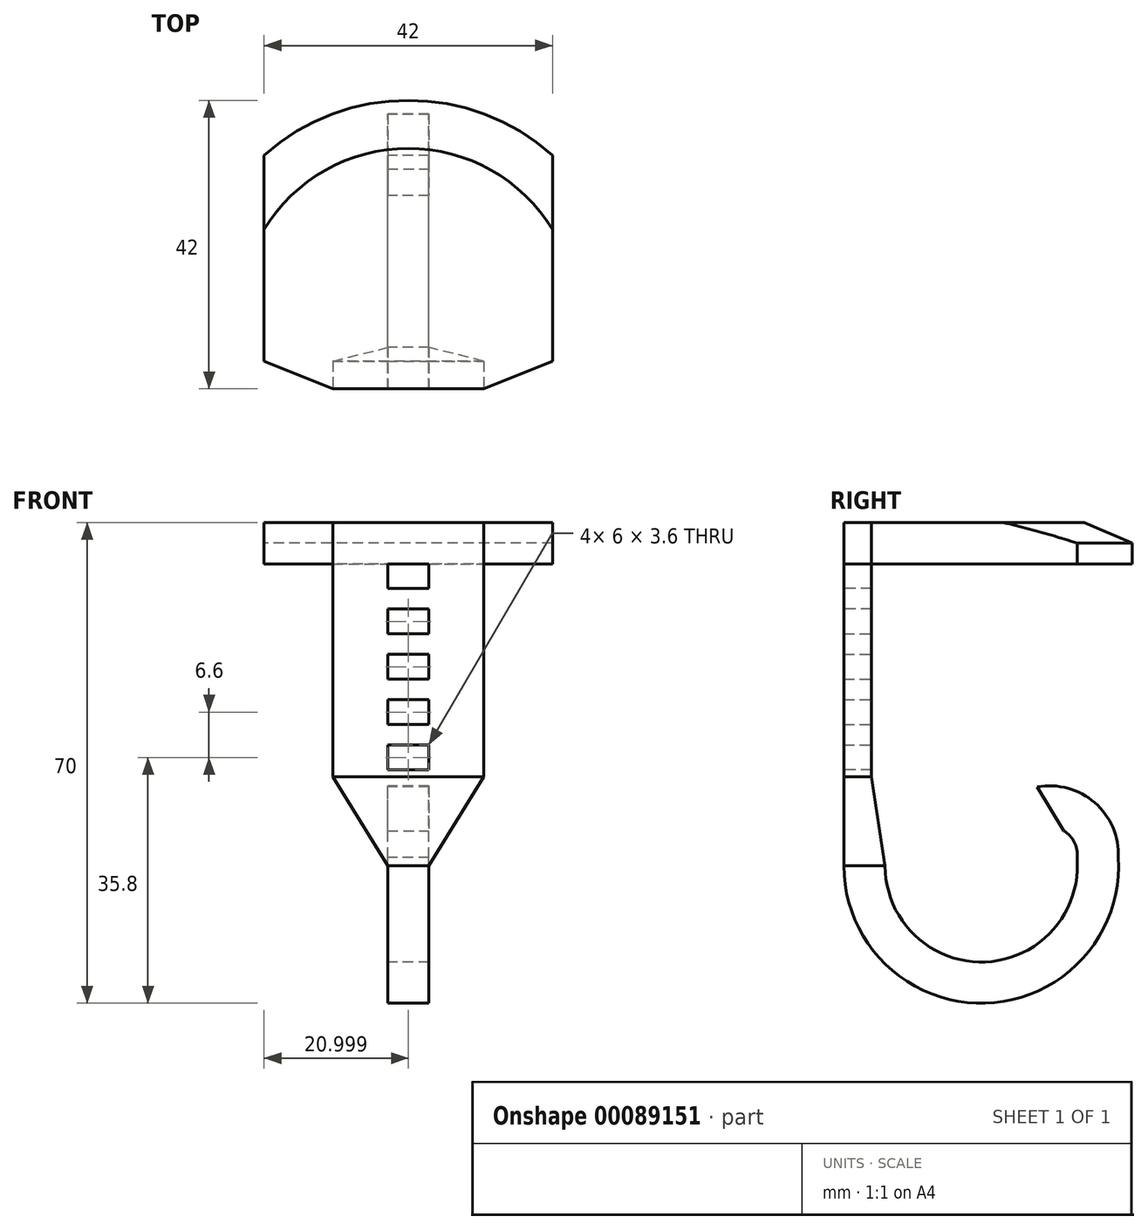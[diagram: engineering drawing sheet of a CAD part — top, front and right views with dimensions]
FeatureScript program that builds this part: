
annotation { "Feature Type Name" : "Feature", "Feature Type Description" : "" }
export const myFeature = defineFeature(function(context is Context, id is Id, definition is map)
    precondition{}
    {
        {
            var Q0;
            Q0=qCreatedBy(makeId("Top.planeOp"),FACE);
            var sketch = newSketch(context, id + "F0", { "sketchPlane" : qUnion([Q0])});
            skLineSegment(sketch, "E0.bottom", {"start": v(-37.77, 36.59) * mm, "end": v(4.23, 36.59) * mm});
            skLineSegment(sketch, "E0.top", {"start": v(-37.77, -1.41) * mm, "end": v(4.23, -1.41) * mm});
            skLineSegment(sketch, "E0.left", {"start": v(-37.77, 36.59) * mm, "end": v(-37.77, -1.41) * mm});
            skLineSegment(sketch, "E0.right", {"start": v(4.23, 36.59) * mm, "end": v(4.23, -1.41) * mm});
            skLineSegment(sketch, "E1", {"start": v(-16.77, 36.59) * mm, "end": v(-16.77, -1.41) * mm, "construction": true});
            skArc(sketch, "E2", {"start": v(4.23, 28.59) * mm, "mid": v(-16.77, 36.59) * mm, "end": v(-37.77, 28.59) * mm});
            skLineSegment(sketch, "E3", {"start": v(4.23, 36.59) * mm, "end": v(4.23, 28.59) * mm, "construction": true});
            skLineSegment(sketch, "E4", {"start": v(4.23, 28.59) * mm, "end": v(4.23, 36.59) * mm});
            skLineSegment(sketch, "E5", {"start": v(-37.77, 28.59) * mm, "end": v(-37.77, 36.59) * mm});
            skSolve(sketch);
        }
        {
            var Q0;
            Q0=makeQuery(id+"F0.imprint","IMPRINT",FACE,{"disambiguationData":[TD([[makeQuery(id+"F0.imprint","IMPRINT",EDGE,{"derivedFrom":sQuery(id+"F0.wireOp",EDGE,"E0.top")}),1.0]])]});
            extrude(context, id + "F1", {"entities" : qUnion([Q0]), "depth" : 6 * mm});
        }
        {
            var Q0;
            Q0=makeQuery(id+"F1.opExtrude","CAP_FACE",FACE,{"disambiguationData":[OSD([sQuery(id+"F0.wireOp",EDGE,"E0.bottom"),sQuery(id+"F0.wireOp",EDGE,"E0.top"),sQuery(id+"F0.wireOp",EDGE,"E0.left"),sQuery(id+"F0.wireOp",EDGE,"E0.right")])],"isStart":false});
            var sketch = newSketch(context, id + "F2", { "sketchPlane" : qUnion([Q0])});
            skLineSegment(sketch, "E6.bottom", {"start": v(-19.77, -1.41) * mm, "end": v(-27.77, -1.41) * mm});
            skLineSegment(sketch, "E6.top", {"start": v(-19.77, -5.41) * mm, "end": v(-27.77, -5.41) * mm});
            skLineSegment(sketch, "E6.left", {"start": v(-19.77, -1.41) * mm, "end": v(-19.77, -5.41) * mm});
            skLineSegment(sketch, "E6.right", {"start": v(-27.77, -1.41) * mm, "end": v(-27.77, -5.41) * mm});
            skLineSegment(sketch, "E7.bottom", {"start": v(-13.77, -1.41) * mm, "end": v(-5.77, -1.41) * mm});
            skLineSegment(sketch, "E7.top", {"start": v(-13.77, -5.41) * mm, "end": v(-5.77, -5.41) * mm});
            skLineSegment(sketch, "E7.left", {"start": v(-13.77, -1.41) * mm, "end": v(-13.77, -5.41) * mm});
            skLineSegment(sketch, "E7.right", {"start": v(-5.77, -1.41) * mm, "end": v(-5.77, -5.41) * mm});
            skLineSegment(sketch, "E8", {"start": v(-37.77, -1.41) * mm, "end": v(-27.77, -1.41) * mm, "construction": true});
            skLineSegment(sketch, "E9", {"start": v(-5.77, -1.41) * mm, "end": v(4.23, -1.41) * mm, "construction": true});
            skSolve(sketch);
        }
        {
            var Q0;
            Q0=makeQuery(id+"F2.imprint","IMPRINT",FACE,{"disambiguationData":[TD([[makeQuery(id+"F2.imprint","IMPRINT",EDGE,{"derivedFrom":sQuery(id+"F2.wireOp",EDGE,"E6.bottom")}),-1.0]])]});
            var Q1;
            Q1=makeQuery(id+"F2.imprint","IMPRINT",FACE,{"disambiguationData":[TD([[makeQuery(id+"F2.imprint","IMPRINT",EDGE,{"derivedFrom":sQuery(id+"F2.wireOp",EDGE,"E7.bottom")}),-1.0]])]});
            extrude(context, id + "F3", {"entities" : qUnion([Q0, Q1]), "operationType" : NewBodyOperationType.ADD, "oppositeDirection" : true, "depth" : 36 * mm});
        }
        {
            var Q0;
            {var subQ1=sQuery(id+"F0.wireOp",EDGE,"E0.left");var subQ3=sQuery(id+"F0.wireOp",EDGE,"E0.top");Q0=makeQuery(id+"F3.boolean.opBoolean","SPLIT",FACE,{"disambiguationData":[TD([makeQuery(id+"F1.opExtrude","SWEPT_FACE",FACE,{"disambiguationData":[OSD([subQ1])]})])],"derivedFrom":makeQuery(id+"F1.opExtrude","SWEPT_FACE",FACE,{"disambiguationData":[OSD([subQ3])]})});}
            var Q1;
            {var subQ0=sQuery(id+"F0.wireOp",EDGE,"E0.right");var subQ2=sQuery(id+"F0.wireOp",EDGE,"E0.top");Q1=makeQuery(id+"F3.boolean.opBoolean","SPLIT",FACE,{"disambiguationData":[TD([makeQuery(id+"F1.opExtrude","SWEPT_FACE",FACE,{"disambiguationData":[OSD([subQ0])]})])],"derivedFrom":makeQuery(id+"F1.opExtrude","SWEPT_FACE",FACE,{"disambiguationData":[OSD([subQ2])]})});}
            var Q2;
            {var subQ0=sQuery(id+"F2.wireOp",EDGE,"E6.left");var subQ4=sQuery(id+"F0.wireOp",EDGE,"E0.top");Q2=makeQuery(id+"F3.boolean.opBoolean","SPLIT",FACE,{"disambiguationData":[TD([makeQuery(id+"F3.opExtrude","SWEPT_FACE",FACE,{"disambiguationData":[OSD([subQ0])]})])],"derivedFrom":makeQuery(id+"F1.opExtrude","SWEPT_FACE",FACE,{"disambiguationData":[OSD([subQ4])]})});}
            extrude(context, id + "F4", {"entities" : qUnion([Q0, Q1, Q2]), "operationType" : NewBodyOperationType.ADD, "depth" : 4 * mm});
        }
        {
            var Q0;
            Q0=makeQuery(id+"F4.opExtrude","CAP_EDGE",EDGE,{"disambiguationData":[OSD([sQuery(id+"F0.wireOp",EDGE,"E0.top"),sQuery(id+"F0.wireOp",EDGE,"E0.left")])],"isStart":false});
            var Q1;
            Q1=makeQuery(id+"F4.opExtrude","CAP_EDGE",EDGE,{"disambiguationData":[OSD([sQuery(id+"F0.wireOp",EDGE,"E0.top"),sQuery(id+"F0.wireOp",EDGE,"E0.right")])],"isStart":false});
            chamfer(context, id + "F5", {"entities" : qUnion([Q0, Q1]), "chamferType" : ChamferType.TWO_OFFSETS, "width1" : 10 * mm, "oppositeDirection" : false, "width2" : 4 * mm, "tangentPropagation" : true});
        }
        {
            var Q0;
            Q0=makeQuery(id+"F3.opExtrude","SWEPT_FACE",FACE,{"disambiguationData":[OSD([sQuery(id+"F2.wireOp",EDGE,"E7.left")])]});
            var sketch = newSketch(context, id + "F6", { "sketchPlane" : qUnion([Q0])});
            skLineSegment(sketch, "E10.bottom", {"start": v(1.41, -3.6) * mm, "end": v(5.41, -3.6) * mm});
            skLineSegment(sketch, "E10.top", {"start": v(1.41, -6.6) * mm, "end": v(5.41, -6.6) * mm});
            skLineSegment(sketch, "E10.left", {"start": v(1.41, -3.6) * mm, "end": v(1.41, -6.6) * mm});
            skLineSegment(sketch, "E10.right", {"start": v(5.41, -3.6) * mm, "end": v(5.41, -6.6) * mm});
            skLineSegment(sketch, "E11.bottom", {"start": v(5.41, -10.2) * mm, "end": v(1.41, -10.2) * mm});
            skLineSegment(sketch, "E11.top", {"start": v(5.41, -13.2) * mm, "end": v(1.41, -13.2) * mm});
            skLineSegment(sketch, "E11.left", {"start": v(5.41, -10.2) * mm, "end": v(5.41, -13.2) * mm});
            skLineSegment(sketch, "E11.right", {"start": v(1.41, -10.2) * mm, "end": v(1.41, -13.2) * mm});
            skLineSegment(sketch, "E12.bottom", {"start": v(5.41, -16.8) * mm, "end": v(1.41, -16.8) * mm});
            skLineSegment(sketch, "E12.top", {"start": v(5.41, -19.8) * mm, "end": v(1.41, -19.8) * mm});
            skLineSegment(sketch, "E12.left", {"start": v(5.41, -16.8) * mm, "end": v(5.41, -19.8) * mm});
            skLineSegment(sketch, "E12.right", {"start": v(1.41, -16.8) * mm, "end": v(1.41, -19.8) * mm});
            skLineSegment(sketch, "E13.bottom", {"start": v(5.41, -23.4) * mm, "end": v(1.41, -23.4) * mm});
            skLineSegment(sketch, "E13.top", {"start": v(5.41, -26.4) * mm, "end": v(1.41, -26.4) * mm});
            skLineSegment(sketch, "E13.left", {"start": v(5.41, -23.4) * mm, "end": v(5.41, -26.4) * mm});
            skLineSegment(sketch, "E13.right", {"start": v(1.41, -23.4) * mm, "end": v(1.41, -26.4) * mm});
            skLineSegment(sketch, "E14", {"start": v(3.41, 0) * mm, "end": v(3.41, -3.6) * mm, "construction": true});
            skLineSegment(sketch, "E15", {"start": v(3.41, -6.6) * mm, "end": v(3.41, -10.2) * mm, "construction": true});
            skLineSegment(sketch, "E16", {"start": v(3.41, -19.8) * mm, "end": v(3.41, -23.4) * mm, "construction": true});
            skLineSegment(sketch, "E17", {"start": v(3.41, -26.4) * mm, "end": v(3.41, -30) * mm, "construction": true});
            skLineSegment(sketch, "E18", {"start": v(3.41, -16.8) * mm, "end": v(3.41, -13.2) * mm, "construction": true});
            skSolve(sketch);
        }
        {
            var Q0;
            Q0=makeQuery(id+"F6.imprint","IMPRINT",FACE,{"disambiguationData":[TD([[makeQuery(id+"F6.imprint","IMPRINT",EDGE,{"derivedFrom":sQuery(id+"F6.wireOp",EDGE,"E13.bottom")}),1.0]])]});
            var Q1;
            Q1=makeQuery(id+"F6.imprint","IMPRINT",FACE,{"disambiguationData":[TD([[makeQuery(id+"F6.imprint","IMPRINT",EDGE,{"derivedFrom":sQuery(id+"F6.wireOp",EDGE,"E12.bottom")}),1.0]])]});
            var Q2;
            Q2=makeQuery(id+"F6.imprint","IMPRINT",FACE,{"disambiguationData":[TD([[makeQuery(id+"F6.imprint","IMPRINT",EDGE,{"derivedFrom":sQuery(id+"F6.wireOp",EDGE,"E11.bottom")}),1.0]])]});
            var Q3;
            Q3=makeQuery(id+"F6.imprint","IMPRINT",FACE,{"disambiguationData":[TD([[makeQuery(id+"F6.imprint","IMPRINT",EDGE,{"derivedFrom":sQuery(id+"F6.wireOp",EDGE,"E10.bottom")}),-1.0]])]});
            extrude(context, id + "F7", {"entities" : qUnion([Q0, Q1, Q2, Q3]), "operationType" : NewBodyOperationType.ADD, "endBound" : BoundingType.UP_TO_NEXT, "depth" : 25 * mm});
        }
        {
            var Q0;
            Q0=sQuery(id+"F0.wireOp",EDGE,"E1");
            cPlane(context, id + "F8", {"entities" : qUnion([Q0]), "cplaneType" : CPlaneType.LINE_ANGLE, "offset" : 150 * mm, "angle" : 90 * degree, "width" : 150 * mm, "height" : 150 * mm});
        }
        {
            var Q0;
            Q0=qCreatedBy(id+"F8.planeOp",FACE);
            var sketch = newSketch(context, id + "F9", { "sketchPlane" : qUnion([Q0])});
            skPoint(sketch, "E19.0", {"position": v(-1.41, -30) * mm});
            skPoint(sketch, "E20.0", {"position": v(-5.41, -30) * mm});
            skArc(sketch, "E21.0", {"start": v(34.55, -42.8) * mm, "mid": v(24.52, -32.33) * mm, "end": v(14.57, -42.86) * mm});
            skArc(sketch, "E21.1", {"start": v(-5.41, -44) * mm, "mid": v(15.2, -64) * mm, "end": v(34.55, -42.8) * mm});
            skLineSegment(sketch, "E22", {"start": v(-5.41, -30) * mm, "end": v(-5.41, -44) * mm, "construction": true});
            skArc(sketch, "E23.0", {"start": v(28.53, -42.8) * mm, "mid": v(24.52, -38.33) * mm, "end": v(20.6, -42.86) * mm});
            skArc(sketch, "E23.1", {"start": v(0.59, -44) * mm, "mid": v(15.2, -57.99) * mm, "end": v(28.53, -42.8) * mm});
            skLineSegment(sketch, "E24", {"start": v(20.6, -42.86) * mm, "end": v(14.57, -42.86) * mm});
            skLineSegment(sketch, "E25", {"start": v(0.59, -44) * mm, "end": v(-5.41, -44) * mm});
            skLineSegment(sketch, "E26", {"start": v(28.53, -42.8) * mm, "end": v(34.55, -42.8) * mm, "construction": true});
            skSolve(sketch);
        }
        {
            var Q0;
            Q0=makeQuery(id+"F9.imprint","IMPRINT",FACE,{"disambiguationData":[TD([[makeQuery(id+"F9.imprint","IMPRINT",EDGE,{"derivedFrom":sQuery(id+"F9.wireOp",EDGE,"E21.0")}),1.0]])]});
            extrude(context, id + "F10", {"entities" : qUnion([Q0]), "endBound" : BoundingType.SYMMETRIC, "depth" : 6 * mm});
        }
        {
            var Q0;
            Q0=makeQuery(id+"F3.opExtrude","CAP_FACE",FACE,{"disambiguationData":[OSD([sQuery(id+"F2.wireOp",EDGE,"E6.bottom"),sQuery(id+"F2.wireOp",EDGE,"E6.top"),sQuery(id+"F2.wireOp",EDGE,"E6.left"),sQuery(id+"F2.wireOp",EDGE,"E6.right")])],"isStart":false});
            var sketch = newSketch(context, id + "F11", { "sketchPlane" : qUnion([Q0])});
            skLineSegment(sketch, "E27.0", {"start": v(-5.77, 1.41) * mm, "end": v(-5.77, 5.41) * mm});
            skLineSegment(sketch, "E28.0", {"start": v(-27.77, 1.41) * mm, "end": v(-27.77, 5.41) * mm});
            skLineSegment(sketch, "E29", {"start": v(-5.77, 1.41) * mm, "end": v(-27.77, 1.41) * mm});
            skLineSegment(sketch, "E30", {"start": v(-27.77, 5.41) * mm, "end": v(-5.77, 5.41) * mm});
            skSolve(sketch);
        }
        {
            var Q0;
            {var subQ0=sQuery(id+"F11.wireOp",EDGE,"E27.0");Q0=makeQuery(id+"F11.imprint","IMPRINT",FACE,{"disambiguationData":[TD([[makeQuery(id+"F11.imprint","IMPRINT",EDGE,{"derivedFrom":subQ0}),1.0]])]});}
            var Q1;
            {var subQ0=sQuery(id+"F11.wireOp",EDGE,"E28.0");Q1=makeQuery(id+"F11.imprint","IMPRINT",FACE,{"disambiguationData":[TD([[makeQuery(id+"F11.imprint","IMPRINT",EDGE,{"derivedFrom":subQ0}),-1.0]])]});}
            extrude(context, id + "F12", {"entities" : qUnion([Q0, Q1]), "operationType" : NewBodyOperationType.ADD, "depth" : 1 * mm});
        }
        {
            var Q0;
            Q0=makeQuery(id+"F12.opExtrude","CAP_FACE",FACE,{"disambiguationData":[OSD([sQuery(id+"F11.wireOp",EDGE,"E27.0"),sQuery(id+"F11.wireOp",EDGE,"E28.0"),sQuery(id+"F11.wireOp",EDGE,"E29"),sQuery(id+"F11.wireOp",EDGE,"E30")])],"isStart":false});
            var Q1;
            Q1=makeQuery(id+"F10.opExtrude","SWEPT_FACE",FACE,{"disambiguationData":[OSD([sQuery(id+"F9.wireOp",EDGE,"E25")])]});
            loft(context, id + "F13", {"sheetProfilesArray" : [{ "sheetProfileEntities" : qUnion([Q0]) }, { "sheetProfileEntities" : qUnion([Q1]) }]});
        }
        {
            var Q0;
            Q0=makeQuery(id+"F10.opExtrude","CAP_FACE",FACE,{"disambiguationData":[OSD([sQuery(id+"F9.wireOp",EDGE,"E21.0"),sQuery(id+"F9.wireOp",EDGE,"E21.1"),sQuery(id+"F9.wireOp",EDGE,"E23.0"),sQuery(id+"F9.wireOp",EDGE,"E23.1"),sQuery(id+"F9.wireOp",EDGE,"E24"),sQuery(id+"F9.wireOp",EDGE,"E25")])],"isStart":false});
            var sketch = newSketch(context, id + "F14", { "sketchPlane" : qUnion([Q0])});
            skLineSegment(sketch, "E31", {"start": v(21.86, -31.05) * mm, "end": v(26.59, -38.89) * mm});
            skLineSegment(sketch, "E32", {"start": v(26.59, -38.89) * mm, "end": v(20.6, -42.86) * mm});
            skLineSegment(sketch, "E33", {"start": v(20.6, -42.86) * mm, "end": v(14.57, -42.86) * mm});
            skLineSegment(sketch, "E34", {"start": v(14.57, -42.86) * mm, "end": v(14.09, -33.68) * mm});
            skLineSegment(sketch, "E35", {"start": v(14.09, -33.68) * mm, "end": v(21.86, -31.05) * mm});
            skSolve(sketch);
        }
        {
            var Q0;
            {var subQ0=sQuery(id+"F14.wireOp",EDGE,"E34");Q0=makeQuery(id+"F14.imprint","IMPRINT",FACE,{"disambiguationData":[TD([[makeQuery(id+"F14.imprint","IMPRINT",EDGE,{"derivedFrom":subQ0}),-1.0]])]});}
            var Q1;
            {var subQ0=sQuery(id+"F14.wireOp",EDGE,"E31");Q1=makeQuery(id+"F14.imprint","IMPRINT",FACE,{"disambiguationData":[TD([[makeQuery(id+"F14.imprint","IMPRINT",EDGE,{"derivedFrom":subQ0}),-1.0]])]});}
            extrude(context, id + "F15", {"entities" : qUnion([Q0, Q1]), "operationType" : NewBodyOperationType.REMOVE, "endBound" : BoundingType.UP_TO_NEXT, "oppositeDirection" : true, "depth" : 25 * mm});
        }
        {
            var Q0;
            Q0=makeQuery(id+"F1.opExtrude","CAP_EDGE",EDGE,{"disambiguationData":[OSD([sQuery(id+"F0.wireOp",EDGE,"E2")])],"isStart":false});
            chamfer(context, id + "F16", {"entities" : qUnion([Q0]), "chamferType" : ChamferType.TWO_OFFSETS, "width1" : 7 * mm, "oppositeDirection" : false, "width2" : 3 * mm, "tangentPropagation" : true});
        }
    });
